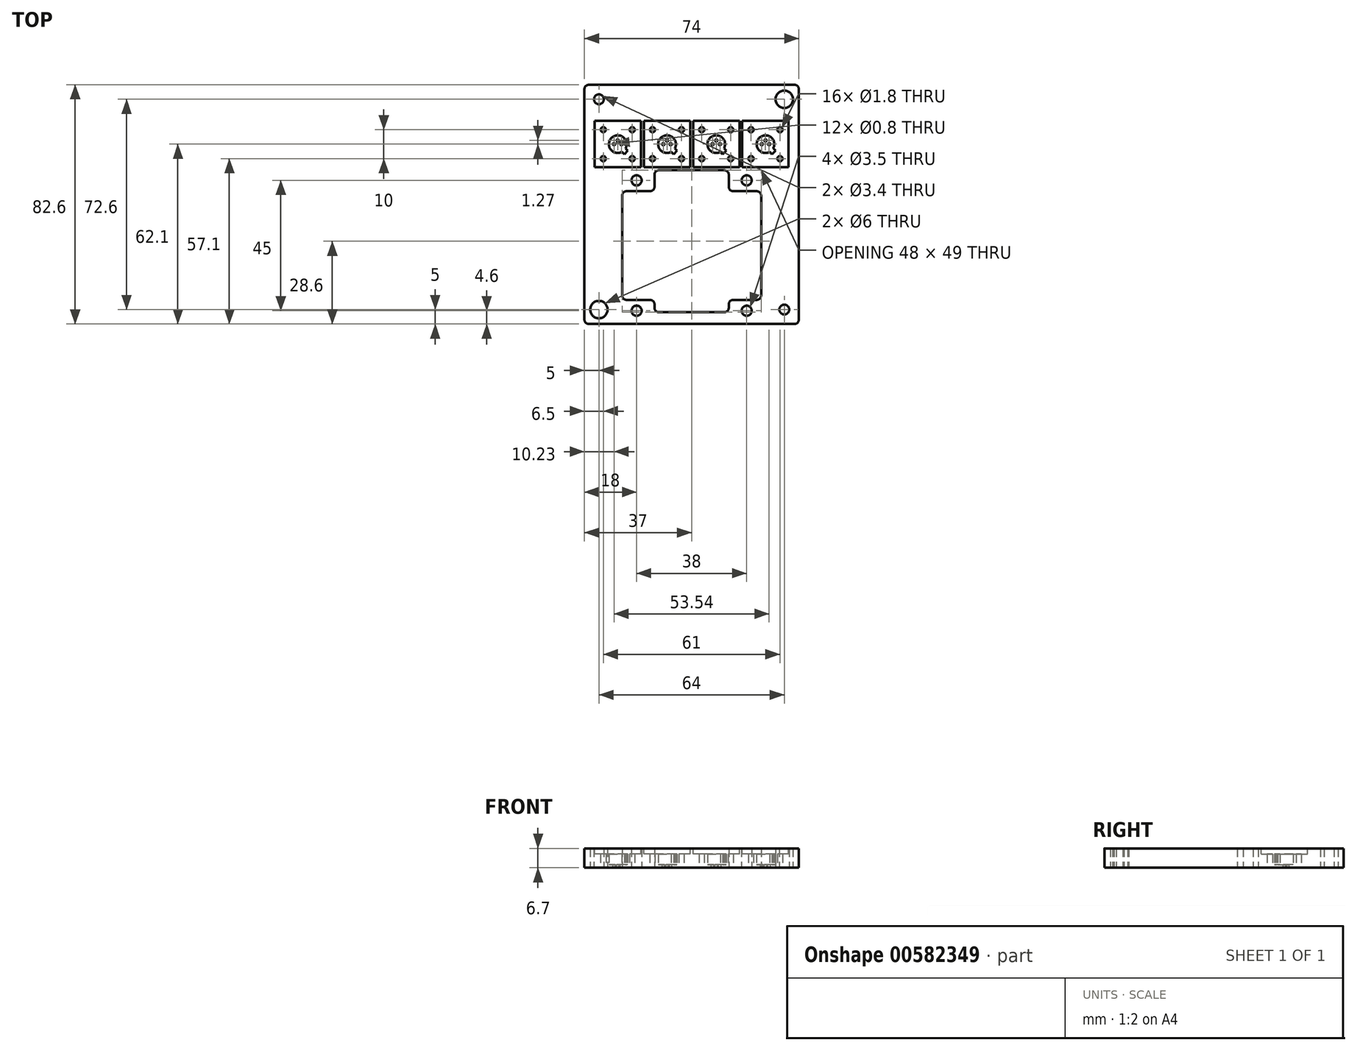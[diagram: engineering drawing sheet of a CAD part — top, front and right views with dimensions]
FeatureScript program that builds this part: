
annotation { "Feature Type Name" : "Feature", "Feature Type Description" : "" }
export const myFeature = defineFeature(function(context is Context, id is Id, definition is map)
    precondition{}
    {
        {
            var Q0;
            Q0=qCreatedBy(makeId("Top.planeOp"),FACE);
            var sketch = newSketch(context, id + "F0", { "sketchPlane" : qUnion([Q0])});
            skLineSegment(sketch, "E0.bottom", {"start": v(22.5, -9) * mm, "end": v(22.5, -61) * mm, "construction": true});
            skLineSegment(sketch, "E0.top", {"start": v(-22.5, -9) * mm, "end": v(-22.5, -61) * mm, "construction": true});
            skLineSegment(sketch, "E0.left", {"start": v(22.5, -9) * mm, "end": v(-22.5, -9) * mm, "construction": true});
            skLineSegment(sketch, "E0.right", {"start": v(22.5, -61) * mm, "end": v(-22.5, -61) * mm, "construction": true});
            skPoint(sketch, "E0.middle", {"position": v(0, -35) * mm});
            skCircle(sketch, "E1", {"center": v(-19, -57.5) * mm, "radius": 1.5 * mm, "construction": true});
            skCircle(sketch, "E2.cCircle", {"center": v(-19, -57.5) * mm, "radius": 2.75 * mm, "construction": true});
            skLineSegment(sketch, "E2.0", {"start": v(-20.59, -54.75) * mm, "end": v(-17.41, -54.75) * mm, "construction": true});
            skLineSegment(sketch, "E2.1", {"start": v(-17.41, -54.75) * mm, "end": v(-15.82, -57.5) * mm, "construction": true});
            skLineSegment(sketch, "E2.2", {"start": v(-15.82, -57.5) * mm, "end": v(-17.41, -60.25) * mm, "construction": true});
            skLineSegment(sketch, "E2.3", {"start": v(-17.41, -60.25) * mm, "end": v(-20.59, -60.25) * mm, "construction": true});
            skLineSegment(sketch, "E2.4", {"start": v(-20.59, -60.25) * mm, "end": v(-22.18, -57.5) * mm, "construction": true});
            skLineSegment(sketch, "E2.5", {"start": v(-22.18, -57.5) * mm, "end": v(-20.59, -54.75) * mm, "construction": true});
            skPoint(sketch, "E2.0.midPoint", {"position": v(-19, -54.75) * mm});
            skLineSegment(sketch, "E3.MirrorCS", {"start": v(-20.59, -15.25) * mm, "end": v(-17.41, -15.25) * mm, "construction": true});
            skCircle(sketch, "E4.MirrorC", {"center": v(-19, -12.5) * mm, "radius": 1.5 * mm, "construction": true});
            skCircle(sketch, "E5.MirrorC", {"center": v(-19, -12.5) * mm, "radius": 2.75 * mm, "construction": true});
            skLineSegment(sketch, "E6.MirrorCS", {"start": v(-17.41, -15.25) * mm, "end": v(-15.82, -12.5) * mm, "construction": true});
            skPoint(sketch, "E7.MirrorP", {"position": v(-19, -15.25) * mm});
            skLineSegment(sketch, "E8.MirrorCS", {"start": v(-22.18, -12.5) * mm, "end": v(-20.59, -15.25) * mm, "construction": true});
            skLineSegment(sketch, "E9.MirrorCS", {"start": v(-20.59, -9.75) * mm, "end": v(-22.18, -12.5) * mm, "construction": true});
            skLineSegment(sketch, "E10.MirrorCS", {"start": v(-15.82, -12.5) * mm, "end": v(-17.41, -9.75) * mm, "construction": true});
            skLineSegment(sketch, "E11.MirrorCS", {"start": v(-17.41, -9.75) * mm, "end": v(-20.59, -9.75) * mm, "construction": true});
            skLineSegment(sketch, "E12.MirrorCS", {"start": v(20.59, -15.25) * mm, "end": v(17.41, -15.25) * mm, "construction": true});
            skLineSegment(sketch, "E13.MirrorCS", {"start": v(22.18, -57.5) * mm, "end": v(20.59, -54.75) * mm, "construction": true});
            skLineSegment(sketch, "E14.MirrorCS", {"start": v(20.59, -60.25) * mm, "end": v(22.18, -57.5) * mm, "construction": true});
            skLineSegment(sketch, "E15.MirrorCS", {"start": v(15.82, -57.5) * mm, "end": v(17.41, -60.25) * mm, "construction": true});
            skLineSegment(sketch, "E16.MirrorCS", {"start": v(17.41, -54.75) * mm, "end": v(15.82, -57.5) * mm, "construction": true});
            skLineSegment(sketch, "E17.MirrorCS", {"start": v(20.59, -54.75) * mm, "end": v(17.41, -54.75) * mm, "construction": true});
            skLineSegment(sketch, "E18.MirrorCS", {"start": v(20.59, -9.75) * mm, "end": v(22.18, -12.5) * mm, "construction": true});
            skLineSegment(sketch, "E19.MirrorCS", {"start": v(17.41, -9.75) * mm, "end": v(20.59, -9.75) * mm, "construction": true});
            skLineSegment(sketch, "E20.MirrorCS", {"start": v(22.18, -12.5) * mm, "end": v(20.59, -15.25) * mm, "construction": true});
            skLineSegment(sketch, "E21.MirrorCS", {"start": v(15.82, -12.5) * mm, "end": v(17.41, -9.75) * mm, "construction": true});
            skLineSegment(sketch, "E22.MirrorCS", {"start": v(17.41, -15.25) * mm, "end": v(15.82, -12.5) * mm, "construction": true});
            skLineSegment(sketch, "E23.MirrorCS", {"start": v(17.41, -60.25) * mm, "end": v(20.59, -60.25) * mm, "construction": true});
            skCircle(sketch, "E24.MirrorC", {"center": v(19, -57.5) * mm, "radius": 2.75 * mm, "construction": true});
            skPoint(sketch, "E25.MirrorP", {"position": v(19, -15.25) * mm});
            skCircle(sketch, "E26.MirrorC", {"center": v(19, -57.5) * mm, "radius": 1.5 * mm, "construction": true});
            skCircle(sketch, "E27.MirrorC", {"center": v(19, -12.5) * mm, "radius": 2.75 * mm, "construction": true});
            skCircle(sketch, "E28.MirrorC", {"center": v(19, -12.5) * mm, "radius": 1.5 * mm, "construction": true});
            skPoint(sketch, "E29.MirrorP", {"position": v(19, -54.75) * mm});
            skSolve(sketch);
        }
        {
            var Q0;
            Q0=qCreatedBy(makeId("Top.planeOp"),FACE);
            var sketch = newSketch(context, id + "F1", { "sketchPlane" : qUnion([Q0])});
            skCircle(sketch, "E30", {"center": v(-25.5, 1.27) * mm, "radius": 0.4 * mm});
            skCircle(sketch, "E31", {"center": v(-24.23, 0) * mm, "radius": 0.4 * mm});
            skCircle(sketch, "E32", {"center": v(-26.77, 0) * mm, "radius": 0.4 * mm});
            skLineSegment(sketch, "E33.bottom", {"start": v(-18, -7.5) * mm, "end": v(-33, -7.5) * mm, "construction": true});
            skLineSegment(sketch, "E33.top", {"start": v(-18, 7.5) * mm, "end": v(-33, 7.5) * mm, "construction": true});
            skLineSegment(sketch, "E33.left", {"start": v(-18, -7.5) * mm, "end": v(-18, 7.5) * mm, "construction": true});
            skLineSegment(sketch, "E33.right", {"start": v(-33, -7.5) * mm, "end": v(-33, 7.5) * mm, "construction": true});
            skPoint(sketch, "E33.middle", {"position": v(-25.5, 0) * mm});
            skCircle(sketch, "E34", {"center": v(-30.5, 5) * mm, "radius": 0.9 * mm});
            skCircle(sketch, "E35.MirrorC", {"center": v(-20.5, 5) * mm, "radius": 0.9 * mm});
            skCircle(sketch, "E36.MirrorC", {"center": v(-30.5, -5) * mm, "radius": 0.9 * mm});
            skCircle(sketch, "E37.MirrorC", {"center": v(-20.5, -5) * mm, "radius": 0.9 * mm});
            skCircle(sketch, "E38.1.0.0", {"center": v(-13.5, -5) * mm, "radius": 0.9 * mm});
            skCircle(sketch, "E38.1.0.1", {"center": v(-13.5, 5) * mm, "radius": 0.9 * mm});
            skLineSegment(sketch, "E38.1.0.2", {"start": v(-16, -7.5) * mm, "end": v(-16, 7.5) * mm, "construction": true});
            skLineSegment(sketch, "E38.1.0.3", {"start": v(-1, -7.5) * mm, "end": v(-1, 7.5) * mm, "construction": true});
            skCircle(sketch, "E38.1.0.4", {"center": v(-3.5, 5) * mm, "radius": 0.9 * mm});
            skCircle(sketch, "E38.1.0.5", {"center": v(-3.5, -5) * mm, "radius": 0.9 * mm});
            skLineSegment(sketch, "E38.1.0.6", {"start": v(-1, -7.5) * mm, "end": v(-16, -7.5) * mm, "construction": true});
            skLineSegment(sketch, "E38.1.0.7", {"start": v(-1, 7.5) * mm, "end": v(-16, 7.5) * mm, "construction": true});
            skPoint(sketch, "E38.1.0.9", {"position": v(-8.5, 0) * mm});
            skCircle(sketch, "E38.1.0.10", {"center": v(-7.23, 0) * mm, "radius": 0.4 * mm});
            skCircle(sketch, "E38.1.0.11", {"center": v(-9.77, 0) * mm, "radius": 0.4 * mm});
            skCircle(sketch, "E38.1.0.12", {"center": v(-8.5, 1.27) * mm, "radius": 0.4 * mm});
            skCircle(sketch, "E38.2.0.0", {"center": v(3.5, -5) * mm, "radius": 0.9 * mm});
            skCircle(sketch, "E38.2.0.1", {"center": v(3.5, 5) * mm, "radius": 0.9 * mm});
            skLineSegment(sketch, "E38.2.0.2", {"start": v(1, -7.5) * mm, "end": v(1, 7.5) * mm, "construction": true});
            skLineSegment(sketch, "E38.2.0.3", {"start": v(16, -7.5) * mm, "end": v(16, 7.5) * mm, "construction": true});
            skCircle(sketch, "E38.2.0.4", {"center": v(13.5, 5) * mm, "radius": 0.9 * mm});
            skCircle(sketch, "E38.2.0.5", {"center": v(13.5, -5) * mm, "radius": 0.9 * mm});
            skLineSegment(sketch, "E38.2.0.6", {"start": v(16, -7.5) * mm, "end": v(1, -7.5) * mm, "construction": true});
            skLineSegment(sketch, "E38.2.0.7", {"start": v(16, 7.5) * mm, "end": v(1, 7.5) * mm, "construction": true});
            skPoint(sketch, "E38.2.0.9", {"position": v(8.5, 0) * mm});
            skCircle(sketch, "E38.2.0.10", {"center": v(9.77, 0) * mm, "radius": 0.4 * mm});
            skCircle(sketch, "E38.2.0.11", {"center": v(7.23, 0) * mm, "radius": 0.4 * mm});
            skCircle(sketch, "E38.2.0.12", {"center": v(8.5, 1.27) * mm, "radius": 0.4 * mm});
            skCircle(sketch, "E38.3.0.0", {"center": v(20.5, -5) * mm, "radius": 0.9 * mm});
            skCircle(sketch, "E38.3.0.1", {"center": v(20.5, 5) * mm, "radius": 0.9 * mm});
            skLineSegment(sketch, "E38.3.0.2", {"start": v(18, -7.5) * mm, "end": v(18, 7.5) * mm, "construction": true});
            skLineSegment(sketch, "E38.3.0.3", {"start": v(33, -7.5) * mm, "end": v(33, 7.5) * mm, "construction": true});
            skCircle(sketch, "E38.3.0.4", {"center": v(30.5, 5) * mm, "radius": 0.9 * mm});
            skCircle(sketch, "E38.3.0.5", {"center": v(30.5, -5) * mm, "radius": 0.9 * mm});
            skLineSegment(sketch, "E38.3.0.6", {"start": v(33, -7.5) * mm, "end": v(18, -7.5) * mm, "construction": true});
            skLineSegment(sketch, "E38.3.0.7", {"start": v(33, 7.5) * mm, "end": v(18, 7.5) * mm, "construction": true});
            skPoint(sketch, "E38.3.0.9", {"position": v(25.5, 0) * mm});
            skCircle(sketch, "E38.3.0.10", {"center": v(26.77, 0) * mm, "radius": 0.4 * mm});
            skCircle(sketch, "E38.3.0.11", {"center": v(24.23, 0) * mm, "radius": 0.4 * mm});
            skCircle(sketch, "E38.3.0.12", {"center": v(25.5, 1.27) * mm, "radius": 0.4 * mm});
            skLineSegment(sketch, "E38.direction1", {"start": v(-33, -7.5) * mm, "end": v(-16, -7.5) * mm, "construction": true});
            skLineSegment(sketch, "E39.top", {"start": v(-37, -62.1) * mm, "end": v(37, -62.1) * mm});
            skLineSegment(sketch, "E39.left", {"start": v(-37, 10.5) * mm, "end": v(-37, -62.1) * mm});
            skLineSegment(sketch, "E39.right", {"start": v(37, 10.5) * mm, "end": v(37, -62.1) * mm});
            skLineSegment(sketch, "E40.bottom", {"start": v(-24, -16.25) * mm, "end": v(-12.82, -16.25) * mm});
            skLineSegment(sketch, "E40.top", {"start": v(-24, -53.75) * mm, "end": v(-12.82, -53.75) * mm});
            skLineSegment(sketch, "E40.left", {"start": v(-24, -16.25) * mm, "end": v(-24, -53.75) * mm});
            skLineSegment(sketch, "E40.right", {"start": v(24, -16.25) * mm, "end": v(24, -53.75) * mm});
            skLineSegment(sketch, "E41.bottom", {"start": v(-12.82, -9) * mm, "end": v(12.82, -9) * mm});
            skLineSegment(sketch, "E41.top", {"start": v(-12.82, -58) * mm, "end": v(12.82, -58) * mm});
            skLineSegment(sketch, "E41.left", {"start": v(-12.82, -9) * mm, "end": v(-12.82, -16.25) * mm});
            skLineSegment(sketch, "E41.right", {"start": v(12.82, -9) * mm, "end": v(12.82, -16.25) * mm});
            skLineSegment(sketch, "E42.trimOffspring", {"start": v(12.82, -53.75) * mm, "end": v(24, -53.75) * mm});
            skLineSegment(sketch, "E43.trimOffspring", {"start": v(-12.82, -53.75) * mm, "end": v(-12.82, -58) * mm});
            skLineSegment(sketch, "E44.trimOffspring", {"start": v(12.82, -53.75) * mm, "end": v(12.82, -58) * mm});
            skLineSegment(sketch, "E45.trimOffspring", {"start": v(12.82, -16.25) * mm, "end": v(24, -16.25) * mm});
            skPoint(sketch, "E46.0", {"position": v(-19, -12.5) * mm});
            skCircle(sketch, "E47", {"center": v(-19, -12.5) * mm, "radius": 1.75 * mm});
            skCircle(sketch, "E48.MirrorC", {"center": v(19, -12.5) * mm, "radius": 1.75 * mm});
            skLineSegment(sketch, "E49", {"start": v(-24, -35) * mm, "end": v(24, -35) * mm, "construction": true});
            skCircle(sketch, "E50.MirrorC", {"center": v(19, -57.5) * mm, "radius": 1.75 * mm});
            skCircle(sketch, "E51.MirrorC", {"center": v(-19, -57.5) * mm, "radius": 1.75 * mm});
            skArc(sketch, "E52", {"start": v(-23.98, 2.23) * mm, "mid": v(-27.4, -1.9) * mm, "end": v(-23.27, 1.52) * mm, "construction": true});
            skLineSegment(sketch, "E53", {"start": v(-22.88, 2.62) * mm, "end": v(-22.53, 2.26) * mm, "construction": true});
            skLineSegment(sketch, "E54", {"start": v(-22.53, 2.26) * mm, "end": v(-23.27, 1.52) * mm, "construction": true});
            skLineSegment(sketch, "E55", {"start": v(-22.88, 2.62) * mm, "end": v(-23.24, 2.97) * mm, "construction": true});
            skLineSegment(sketch, "E56", {"start": v(-23.24, 2.97) * mm, "end": v(-23.98, 2.23) * mm, "construction": true});
            skLineSegment(sketch, "E57.0", {"start": v(-23.24, -3.46) * mm, "end": v(-24.03, -2.67) * mm});
            skArc(sketch, "E57.1", {"start": v(-22.83, -1.47) * mm, "mid": v(-27.66, 2.16) * mm, "end": v(-24.03, -2.67) * mm});
            skLineSegment(sketch, "E57.2", {"start": v(-22.64, -2.86) * mm, "end": v(-23.24, -3.46) * mm});
            skLineSegment(sketch, "E57.3", {"start": v(-22.64, -2.86) * mm, "end": v(-22.04, -2.26) * mm});
            skLineSegment(sketch, "E57.4", {"start": v(-22.04, -2.26) * mm, "end": v(-22.83, -1.47) * mm});
            skArc(sketch, "E58.1.0.0", {"start": v(-5.83, -1.47) * mm, "mid": v(-10.66, 2.16) * mm, "end": v(-7.03, -2.67) * mm});
            skLineSegment(sketch, "E58.1.0.1", {"start": v(-5.04, -2.26) * mm, "end": v(-5.83, -1.47) * mm});
            skLineSegment(sketch, "E58.1.0.2", {"start": v(-5.64, -2.86) * mm, "end": v(-5.04, -2.26) * mm});
            skLineSegment(sketch, "E58.1.0.3", {"start": v(-6.24, -3.46) * mm, "end": v(-7.03, -2.67) * mm});
            skLineSegment(sketch, "E58.1.0.4", {"start": v(-5.64, -2.86) * mm, "end": v(-6.24, -3.46) * mm});
            skArc(sketch, "E58.2.0.0", {"start": v(11.17, -1.47) * mm, "mid": v(6.34, 2.16) * mm, "end": v(9.97, -2.67) * mm});
            skLineSegment(sketch, "E58.2.0.1", {"start": v(11.96, -2.26) * mm, "end": v(11.17, -1.47) * mm});
            skLineSegment(sketch, "E58.2.0.2", {"start": v(11.36, -2.86) * mm, "end": v(11.96, -2.26) * mm});
            skLineSegment(sketch, "E58.2.0.3", {"start": v(10.76, -3.46) * mm, "end": v(9.97, -2.67) * mm});
            skLineSegment(sketch, "E58.2.0.4", {"start": v(11.36, -2.86) * mm, "end": v(10.76, -3.46) * mm});
            skArc(sketch, "E58.3.0.0", {"start": v(28.17, -1.47) * mm, "mid": v(23.34, 2.16) * mm, "end": v(26.97, -2.67) * mm});
            skLineSegment(sketch, "E58.3.0.1", {"start": v(28.96, -2.26) * mm, "end": v(28.17, -1.47) * mm});
            skLineSegment(sketch, "E58.3.0.2", {"start": v(28.36, -2.86) * mm, "end": v(28.96, -2.26) * mm});
            skLineSegment(sketch, "E58.3.0.3", {"start": v(27.76, -3.46) * mm, "end": v(26.97, -2.67) * mm});
            skLineSegment(sketch, "E58.3.0.4", {"start": v(28.36, -2.86) * mm, "end": v(27.76, -3.46) * mm});
            skLineSegment(sketch, "E58.direction1", {"start": v(-25.5, 0) * mm, "end": v(-8.5, 0) * mm, "construction": true});
            skLineSegment(sketch, "E59.top", {"start": v(-37, 20.5) * mm, "end": v(37, 20.5) * mm});
            skLineSegment(sketch, "E59.left", {"start": v(-37, 10.5) * mm, "end": v(-37, 20.5) * mm});
            skLineSegment(sketch, "E59.right", {"start": v(37, 10.5) * mm, "end": v(37, 20.5) * mm});
            skCircle(sketch, "E60", {"center": v(-32, 15.5) * mm, "radius": 1.7 * mm});
            skCircle(sketch, "E61", {"center": v(-32, 15.5) * mm, "radius": 3 * mm});
            skCircle(sketch, "E62.MirrorC", {"center": v(32, 15.5) * mm, "radius": 3 * mm});
            skCircle(sketch, "E63.MirrorC", {"center": v(32, 15.5) * mm, "radius": 1.7 * mm});
            skLineSegment(sketch, "E64", {"start": v(-37, -20.8) * mm, "end": v(37, -20.8) * mm, "construction": true});
            skCircle(sketch, "E65.MirrorC", {"center": v(32, -57.1) * mm, "radius": 1.7 * mm});
            skCircle(sketch, "E66.MirrorC", {"center": v(32, -57.1) * mm, "radius": 3 * mm});
            skCircle(sketch, "E67.MirrorC", {"center": v(-32, -57.1) * mm, "radius": 3 * mm});
            skCircle(sketch, "E68.MirrorC", {"center": v(-32, -57.1) * mm, "radius": 1.7 * mm});
            skSolve(sketch);
        }
        {
            var Q0;
            Q0=makeQuery(id+"F1.imprint","IMPRINT",FACE,{"disambiguationData":[TD([[makeQuery(id+"F1.imprint","IMPRINT",EDGE,{"derivedFrom":sQuery(id+"F1.wireOp",EDGE,"E34")}),-1.0]])]});
            var Q1;
            Q1=makeQuery(id+"F1.imprint","IMPRINT",FACE,{"disambiguationData":[TD([[makeQuery(id+"F1.imprint","IMPRINT",EDGE,{"derivedFrom":sQuery(id+"F1.wireOp",EDGE,"E60")}),-1.0]])]});
            var Q2;
            Q2=makeQuery(id+"F1.imprint","IMPRINT",FACE,{"disambiguationData":[TD([[makeQuery(id+"F1.imprint","IMPRINT",EDGE,{"derivedFrom":sQuery(id+"F1.wireOp",EDGE,"E62.MirrorC")}),-1.0]])]});
            var Q3;
            Q3=makeQuery(id+"F1.imprint","IMPRINT",FACE,{"disambiguationData":[TD([[makeQuery(id+"F1.imprint","IMPRINT",EDGE,{"derivedFrom":sQuery(id+"F1.wireOp",EDGE,"E67.MirrorC")}),-1.0]])]});
            var Q4;
            Q4=makeQuery(id+"F1.imprint","IMPRINT",FACE,{"disambiguationData":[TD([[makeQuery(id+"F1.imprint","IMPRINT",EDGE,{"derivedFrom":sQuery(id+"F1.wireOp",EDGE,"E65.MirrorC")}),-1.0]])]});
            extrude(context, id + "F2", {"entities" : qUnion([Q0, Q1, Q2, Q3, Q4]), "depth" : (3.6 + 2.1) * mm, "offsetDistance" : 25 * mm});
        }
        {
            var Q0;
            Q0 = qSketchRegion(id + "F1", true);
            var Q1;
            Q1=makeQuery(id+"F1.imprint","IMPRINT",FACE,{"disambiguationData":[TD([[makeQuery(id+"F1.imprint","IMPRINT",EDGE,{"derivedFrom":sQuery(id+"F1.wireOp",EDGE,"E30")}),-1.0]])]});
            var Q2;
            Q2=makeQuery(id+"F1.imprint","IMPRINT",FACE,{"disambiguationData":[TD([[makeQuery(id+"F1.imprint","IMPRINT",EDGE,{"derivedFrom":sQuery(id+"F1.wireOp",EDGE,"E38.1.0.10")}),-1.0]])]});
            var Q3;
            Q3=makeQuery(id+"F1.imprint","IMPRINT",FACE,{"disambiguationData":[TD([[makeQuery(id+"F1.imprint","IMPRINT",EDGE,{"derivedFrom":sQuery(id+"F1.wireOp",EDGE,"E38.2.0.10")}),-1.0]])]});
            var Q4;
            Q4=makeQuery(id+"F1.imprint","IMPRINT",FACE,{"disambiguationData":[TD([[makeQuery(id+"F1.imprint","IMPRINT",EDGE,{"derivedFrom":sQuery(id+"F1.wireOp",EDGE,"E38.3.0.10")}),-1.0]])]});
            var Q5;
            Q5=makeQuery(id+"F1.imprint","IMPRINT",FACE,{"disambiguationData":[TD([[makeQuery(id+"F1.imprint","IMPRINT",EDGE,{"derivedFrom":sQuery(id+"F1.wireOp",EDGE,"E67.MirrorC")}),-1.0]])]});
            var Q6;
            Q6=makeQuery(id+"F1.imprint","IMPRINT",FACE,{"disambiguationData":[TD([[makeQuery(id+"F1.imprint","IMPRINT",EDGE,{"derivedFrom":sQuery(id+"F1.wireOp",EDGE,"E60")}),-1.0]])]});
            var Q7;
            Q7=makeQuery(id+"F1.imprint","IMPRINT",FACE,{"disambiguationData":[TD([[makeQuery(id+"F1.imprint","IMPRINT",EDGE,{"derivedFrom":sQuery(id+"F1.wireOp",EDGE,"E62.MirrorC")}),-1.0]])]});
            var Q8;
            Q8=makeQuery(id+"F1.imprint","IMPRINT",FACE,{"disambiguationData":[TD([[makeQuery(id+"F1.imprint","IMPRINT",EDGE,{"derivedFrom":sQuery(id+"F1.wireOp",EDGE,"E65.MirrorC")}),-1.0]])]});
            extrude(context, id + "F3", {"entities" : qUnion([Q0, Q1, Q2, Q3, Q4, Q5, Q6, Q7, Q8]), "operationType" : NewBodyOperationType.ADD, "oppositeDirection" : true, "depth" : 1 * mm, "offsetDistance" : 25 * mm});
        }
        {
            var Q0;
            Q0=makeQuery(id+"F2.opExtrude","CAP_FACE",FACE,{"disambiguationData":[OSD([sQuery(id+"F1.wireOp",EDGE,"E34"),sQuery(id+"F1.wireOp",EDGE,"E35.MirrorC"),sQuery(id+"F1.wireOp",EDGE,"E36.MirrorC"),sQuery(id+"F1.wireOp",EDGE,"E37.MirrorC"),sQuery(id+"F1.wireOp",EDGE,"E38.1.0.0"),sQuery(id+"F1.wireOp",EDGE,"E38.1.0.1"),sQuery(id+"F1.wireOp",EDGE,"E38.1.0.4"),sQuery(id+"F1.wireOp",EDGE,"E38.1.0.5"),sQuery(id+"F1.wireOp",EDGE,"E38.2.0.0"),sQuery(id+"F1.wireOp",EDGE,"E38.2.0.1"),sQuery(id+"F1.wireOp",EDGE,"E38.2.0.4"),sQuery(id+"F1.wireOp",EDGE,"E38.2.0.5"),sQuery(id+"F1.wireOp",EDGE,"E38.3.0.0"),sQuery(id+"F1.wireOp",EDGE,"E38.3.0.1"),sQuery(id+"F1.wireOp",EDGE,"E38.3.0.4"),sQuery(id+"F1.wireOp",EDGE,"E38.3.0.5"),sQuery(id+"F1.wireOp",EDGE,"E39.bottom"),sQuery(id+"F1.wireOp",EDGE,"E39.top"),sQuery(id+"F1.wireOp",EDGE,"E39.left"),sQuery(id+"F1.wireOp",EDGE,"E39.right"),sQuery(id+"F1.wireOp",EDGE,"E40.bottom"),sQuery(id+"F1.wireOp",EDGE,"E40.top"),sQuery(id+"F1.wireOp",EDGE,"E40.left"),sQuery(id+"F1.wireOp",EDGE,"E40.right"),sQuery(id+"F1.wireOp",EDGE,"E41.bottom"),sQuery(id+"F1.wireOp",EDGE,"E41.top"),sQuery(id+"F1.wireOp",EDGE,"E41.left"),sQuery(id+"F1.wireOp",EDGE,"E41.right"),sQuery(id+"F1.wireOp",EDGE,"E42.trimOffspring"),sQuery(id+"F1.wireOp",EDGE,"E43.trimOffspring"),sQuery(id+"F1.wireOp",EDGE,"E44.trimOffspring"),sQuery(id+"F1.wireOp",EDGE,"E45.trimOffspring"),sQuery(id+"F1.wireOp",EDGE,"E47"),sQuery(id+"F1.wireOp",EDGE,"E48.MirrorC"),sQuery(id+"F1.wireOp",EDGE,"E50.MirrorC"),sQuery(id+"F1.wireOp",EDGE,"E51.MirrorC"),sQuery(id+"F1.wireOp",EDGE,"E57.0"),sQuery(id+"F1.wireOp",EDGE,"E57.1"),sQuery(id+"F1.wireOp",EDGE,"E57.2"),sQuery(id+"F1.wireOp",EDGE,"E57.3"),sQuery(id+"F1.wireOp",EDGE,"E57.4"),sQuery(id+"F1.wireOp",EDGE,"E58.1.0.0"),sQuery(id+"F1.wireOp",EDGE,"E58.1.0.1"),sQuery(id+"F1.wireOp",EDGE,"E58.1.0.2"),sQuery(id+"F1.wireOp",EDGE,"E58.1.0.3"),sQuery(id+"F1.wireOp",EDGE,"E58.1.0.4"),sQuery(id+"F1.wireOp",EDGE,"E58.2.0.0"),sQuery(id+"F1.wireOp",EDGE,"E58.2.0.1"),sQuery(id+"F1.wireOp",EDGE,"E58.2.0.2"),sQuery(id+"F1.wireOp",EDGE,"E58.2.0.3"),sQuery(id+"F1.wireOp",EDGE,"E58.2.0.4"),sQuery(id+"F1.wireOp",EDGE,"E58.3.0.0"),sQuery(id+"F1.wireOp",EDGE,"E58.3.0.1"),sQuery(id+"F1.wireOp",EDGE,"E58.3.0.2"),sQuery(id+"F1.wireOp",EDGE,"E58.3.0.3"),sQuery(id+"F1.wireOp",EDGE,"E58.3.0.4")])],"isStart":false});
            var sketch = newSketch(context, id + "F4", { "sketchPlane" : qUnion([Q0])});
            skLineSegment(sketch, "E69.bottom", {"start": v(-17.5, -8) * mm, "end": v(-33.5, -8) * mm});
            skLineSegment(sketch, "E69.top", {"start": v(-17.5, 8) * mm, "end": v(-33.5, 8) * mm});
            skLineSegment(sketch, "E69.left", {"start": v(-17.5, -8) * mm, "end": v(-17.5, 8) * mm});
            skLineSegment(sketch, "E69.right", {"start": v(-33.5, -8) * mm, "end": v(-33.5, 8) * mm});
            skPoint(sketch, "E69.middle", {"position": v(-25.5, 0) * mm});
            skPoint(sketch, "E70.1.0.0", {"position": v(-8.5, 0) * mm});
            skLineSegment(sketch, "E70.1.0.1", {"start": v(-16.5, -8) * mm, "end": v(-16.5, 8) * mm});
            skLineSegment(sketch, "E70.1.0.2", {"start": v(-0.5, -8) * mm, "end": v(-0.5, 8) * mm});
            skLineSegment(sketch, "E70.1.0.3", {"start": v(-0.5, 8) * mm, "end": v(-16.5, 8) * mm});
            skLineSegment(sketch, "E70.1.0.4", {"start": v(-0.5, -8) * mm, "end": v(-16.5, -8) * mm});
            skPoint(sketch, "E70.2.0.0", {"position": v(8.5, 0) * mm});
            skLineSegment(sketch, "E70.2.0.1", {"start": v(0.5, -8) * mm, "end": v(0.5, 8) * mm});
            skLineSegment(sketch, "E70.2.0.2", {"start": v(16.5, -8) * mm, "end": v(16.5, 8) * mm});
            skLineSegment(sketch, "E70.2.0.3", {"start": v(16.5, 8) * mm, "end": v(0.5, 8) * mm});
            skLineSegment(sketch, "E70.2.0.4", {"start": v(16.5, -8) * mm, "end": v(0.5, -8) * mm});
            skPoint(sketch, "E70.3.0.0", {"position": v(25.5, 0) * mm});
            skLineSegment(sketch, "E70.3.0.1", {"start": v(17.5, -8) * mm, "end": v(17.5, 8) * mm});
            skLineSegment(sketch, "E70.3.0.2", {"start": v(33.5, -8) * mm, "end": v(33.5, 8) * mm});
            skLineSegment(sketch, "E70.3.0.3", {"start": v(33.5, 8) * mm, "end": v(17.5, 8) * mm});
            skLineSegment(sketch, "E70.3.0.4", {"start": v(33.5, -8) * mm, "end": v(17.5, -8) * mm});
            skLineSegment(sketch, "E70.direction1", {"start": v(-33.5, -8) * mm, "end": v(-16.5, -8) * mm, "construction": true});
            skSolve(sketch);
        }
        {
            var Q0;
            Q0 = qSketchRegion(id + "F4", true);
            extrude(context, id + "F5", {"entities" : qUnion([Q0]), "operationType" : NewBodyOperationType.REMOVE, "oppositeDirection" : true, "depth" : 2 * mm, "offsetDistance" : 25 * mm});
        }
        {
            var Q0;
            {var subQ0=sQuery(id+"F1.wireOp",EDGE,"E41.left");var subQ1=sQuery(id+"F1.wireOp",EDGE,"E40.bottom");Q0=makeQuery(id+"F3.boolean.opBoolean","MERGE",EDGE,{"derivedFrom":[makeQuery(id+"F2.opExtrude","SWEPT_EDGE",EDGE,{"disambiguationData":[OSD([subQ1,subQ0])]}),makeQuery(id+"F3.opExtrude","SWEPT_EDGE",EDGE,{"disambiguationData":[OSD([subQ1,subQ0])]})]});}
            var Q1;
            {var subQ0=sQuery(id+"F1.wireOp",EDGE,"E45.trimOffspring");var subQ1=sQuery(id+"F1.wireOp",EDGE,"E41.right");Q1=makeQuery(id+"F3.boolean.opBoolean","MERGE",EDGE,{"derivedFrom":[makeQuery(id+"F2.opExtrude","SWEPT_EDGE",EDGE,{"disambiguationData":[OSD([subQ1,subQ0])]}),makeQuery(id+"F3.opExtrude","SWEPT_EDGE",EDGE,{"disambiguationData":[OSD([subQ1,subQ0])]})]});}
            var Q2;
            {var subQ0=sQuery(id+"F1.wireOp",EDGE,"E41.left");var subQ1=sQuery(id+"F1.wireOp",EDGE,"E41.bottom");Q2=makeQuery(id+"F3.boolean.opBoolean","MERGE",EDGE,{"derivedFrom":[makeQuery(id+"F2.opExtrude","SWEPT_EDGE",EDGE,{"disambiguationData":[OSD([subQ1,subQ0])]}),makeQuery(id+"F3.opExtrude","SWEPT_EDGE",EDGE,{"disambiguationData":[OSD([subQ1,subQ0])]})]});}
            var Q3;
            {var subQ0=sQuery(id+"F1.wireOp",EDGE,"E41.right");var subQ1=sQuery(id+"F1.wireOp",EDGE,"E41.bottom");Q3=makeQuery(id+"F3.boolean.opBoolean","MERGE",EDGE,{"derivedFrom":[makeQuery(id+"F2.opExtrude","SWEPT_EDGE",EDGE,{"disambiguationData":[OSD([subQ1,subQ0])]}),makeQuery(id+"F3.opExtrude","SWEPT_EDGE",EDGE,{"disambiguationData":[OSD([subQ1,subQ0])]})]});}
            var Q4;
            {var subQ0=sQuery(id+"F1.wireOp",EDGE,"E45.trimOffspring");var subQ1=sQuery(id+"F1.wireOp",EDGE,"E40.right");Q4=makeQuery(id+"F3.boolean.opBoolean","MERGE",EDGE,{"derivedFrom":[makeQuery(id+"F2.opExtrude","SWEPT_EDGE",EDGE,{"disambiguationData":[OSD([subQ1,subQ0])]}),makeQuery(id+"F3.opExtrude","SWEPT_EDGE",EDGE,{"disambiguationData":[OSD([subQ1,subQ0])]})]});}
            var Q5;
            {var subQ0=sQuery(id+"F1.wireOp",EDGE,"E40.left");var subQ1=sQuery(id+"F1.wireOp",EDGE,"E40.bottom");Q5=makeQuery(id+"F3.boolean.opBoolean","MERGE",EDGE,{"derivedFrom":[makeQuery(id+"F2.opExtrude","SWEPT_EDGE",EDGE,{"disambiguationData":[OSD([subQ1,subQ0])]}),makeQuery(id+"F3.opExtrude","SWEPT_EDGE",EDGE,{"disambiguationData":[OSD([subQ1,subQ0])]})]});}
            var Q6;
            {var subQ0=sQuery(id+"F1.wireOp",EDGE,"E40.left");var subQ1=sQuery(id+"F1.wireOp",EDGE,"E40.top");Q6=makeQuery(id+"F3.boolean.opBoolean","MERGE",EDGE,{"derivedFrom":[makeQuery(id+"F2.opExtrude","SWEPT_EDGE",EDGE,{"disambiguationData":[OSD([subQ1,subQ0])]}),makeQuery(id+"F3.opExtrude","SWEPT_EDGE",EDGE,{"disambiguationData":[OSD([subQ1,subQ0])]})]});}
            var Q7;
            {var subQ0=sQuery(id+"F1.wireOp",EDGE,"E43.trimOffspring");var subQ1=sQuery(id+"F1.wireOp",EDGE,"E40.top");Q7=makeQuery(id+"F3.boolean.opBoolean","MERGE",EDGE,{"derivedFrom":[makeQuery(id+"F2.opExtrude","SWEPT_EDGE",EDGE,{"disambiguationData":[OSD([subQ1,subQ0])]}),makeQuery(id+"F3.opExtrude","SWEPT_EDGE",EDGE,{"disambiguationData":[OSD([subQ1,subQ0])]})]});}
            var Q8;
            {var subQ0=sQuery(id+"F1.wireOp",EDGE,"E43.trimOffspring");var subQ1=sQuery(id+"F1.wireOp",EDGE,"E41.top");Q8=makeQuery(id+"F3.boolean.opBoolean","MERGE",EDGE,{"derivedFrom":[makeQuery(id+"F2.opExtrude","SWEPT_EDGE",EDGE,{"disambiguationData":[OSD([subQ1,subQ0])]}),makeQuery(id+"F3.opExtrude","SWEPT_EDGE",EDGE,{"disambiguationData":[OSD([subQ1,subQ0])]})]});}
            var Q9;
            {var subQ0=sQuery(id+"F1.wireOp",EDGE,"E44.trimOffspring");var subQ1=sQuery(id+"F1.wireOp",EDGE,"E41.top");Q9=makeQuery(id+"F3.boolean.opBoolean","MERGE",EDGE,{"derivedFrom":[makeQuery(id+"F2.opExtrude","SWEPT_EDGE",EDGE,{"disambiguationData":[OSD([subQ1,subQ0])]}),makeQuery(id+"F3.opExtrude","SWEPT_EDGE",EDGE,{"disambiguationData":[OSD([subQ1,subQ0])]})]});}
            var Q10;
            {var subQ0=sQuery(id+"F1.wireOp",EDGE,"E44.trimOffspring");var subQ1=sQuery(id+"F1.wireOp",EDGE,"E42.trimOffspring");Q10=makeQuery(id+"F3.boolean.opBoolean","MERGE",EDGE,{"derivedFrom":[makeQuery(id+"F2.opExtrude","SWEPT_EDGE",EDGE,{"disambiguationData":[OSD([subQ1,subQ0])]}),makeQuery(id+"F3.opExtrude","SWEPT_EDGE",EDGE,{"disambiguationData":[OSD([subQ1,subQ0])]})]});}
            var Q11;
            {var subQ0=sQuery(id+"F1.wireOp",EDGE,"E42.trimOffspring");var subQ1=sQuery(id+"F1.wireOp",EDGE,"E40.right");Q11=makeQuery(id+"F3.boolean.opBoolean","MERGE",EDGE,{"derivedFrom":[makeQuery(id+"F2.opExtrude","SWEPT_EDGE",EDGE,{"disambiguationData":[OSD([subQ1,subQ0])]}),makeQuery(id+"F3.opExtrude","SWEPT_EDGE",EDGE,{"disambiguationData":[OSD([subQ1,subQ0])]})]});}
            var Q12;
            {var subQ0=sQuery(id+"F1.wireOp",EDGE,"E39.left");var subQ1=sQuery(id+"F1.wireOp",EDGE,"E39.bottom");Q12=makeQuery(id+"F3.boolean.opBoolean","MERGE",EDGE,{"derivedFrom":[makeQuery(id+"F2.opExtrude","SWEPT_EDGE",EDGE,{"disambiguationData":[OSD([subQ1,subQ0])]}),makeQuery(id+"F3.opExtrude","SWEPT_EDGE",EDGE,{"disambiguationData":[OSD([subQ1,subQ0])]})]});}
            var Q13;
            {var subQ0=sQuery(id+"F1.wireOp",EDGE,"E39.right");var subQ1=sQuery(id+"F1.wireOp",EDGE,"E39.bottom");Q13=makeQuery(id+"F3.boolean.opBoolean","MERGE",EDGE,{"derivedFrom":[makeQuery(id+"F2.opExtrude","SWEPT_EDGE",EDGE,{"disambiguationData":[OSD([subQ1,subQ0])]}),makeQuery(id+"F3.opExtrude","SWEPT_EDGE",EDGE,{"disambiguationData":[OSD([subQ1,subQ0])]})]});}
            var Q14;
            {var subQ0=sQuery(id+"F1.wireOp",EDGE,"E39.right");var subQ1=sQuery(id+"F1.wireOp",EDGE,"E39.top");Q14=makeQuery(id+"F3.boolean.opBoolean","MERGE",EDGE,{"derivedFrom":[makeQuery(id+"F2.opExtrude","SWEPT_EDGE",EDGE,{"disambiguationData":[OSD([subQ1,subQ0])]}),makeQuery(id+"F3.opExtrude","SWEPT_EDGE",EDGE,{"disambiguationData":[OSD([subQ1,subQ0])]})]});}
            var Q15;
            {var subQ0=sQuery(id+"F1.wireOp",EDGE,"E39.left");var subQ1=sQuery(id+"F1.wireOp",EDGE,"E39.top");Q15=makeQuery(id+"F3.boolean.opBoolean","MERGE",EDGE,{"derivedFrom":[makeQuery(id+"F2.opExtrude","SWEPT_EDGE",EDGE,{"disambiguationData":[OSD([subQ1,subQ0])]}),makeQuery(id+"F3.opExtrude","SWEPT_EDGE",EDGE,{"disambiguationData":[OSD([subQ1,subQ0])]})]});}
            var Q16;
            {var subQ0=sQuery(id+"F1.wireOp",EDGE,"E59.left");var subQ1=sQuery(id+"F1.wireOp",EDGE,"E59.top");Q16=makeQuery(id+"F3.boolean.opBoolean","MERGE",EDGE,{"derivedFrom":[makeQuery(id+"F2.opExtrude","SWEPT_EDGE",EDGE,{"disambiguationData":[OSD([subQ1,subQ0])]}),makeQuery(id+"F3.opExtrude","SWEPT_EDGE",EDGE,{"disambiguationData":[OSD([subQ1,subQ0])]})]});}
            var Q17;
            {var subQ0=sQuery(id+"F1.wireOp",EDGE,"E59.right");var subQ1=sQuery(id+"F1.wireOp",EDGE,"E59.top");Q17=makeQuery(id+"F3.boolean.opBoolean","MERGE",EDGE,{"derivedFrom":[makeQuery(id+"F2.opExtrude","SWEPT_EDGE",EDGE,{"disambiguationData":[OSD([subQ1,subQ0])]}),makeQuery(id+"F3.opExtrude","SWEPT_EDGE",EDGE,{"disambiguationData":[OSD([subQ1,subQ0])]})]});}
            fillet(context, id + "F6", {"entities" : qUnion([Q0, Q1, Q2, Q3, Q4, Q5, Q6, Q7, Q8, Q9, Q10, Q11, Q12, Q13, Q14, Q15, Q16, Q17]), "radius" : 1.5 * mm, "tangentPropagation" : true, "allowEdgeOverflow" : false});
        }
    });
